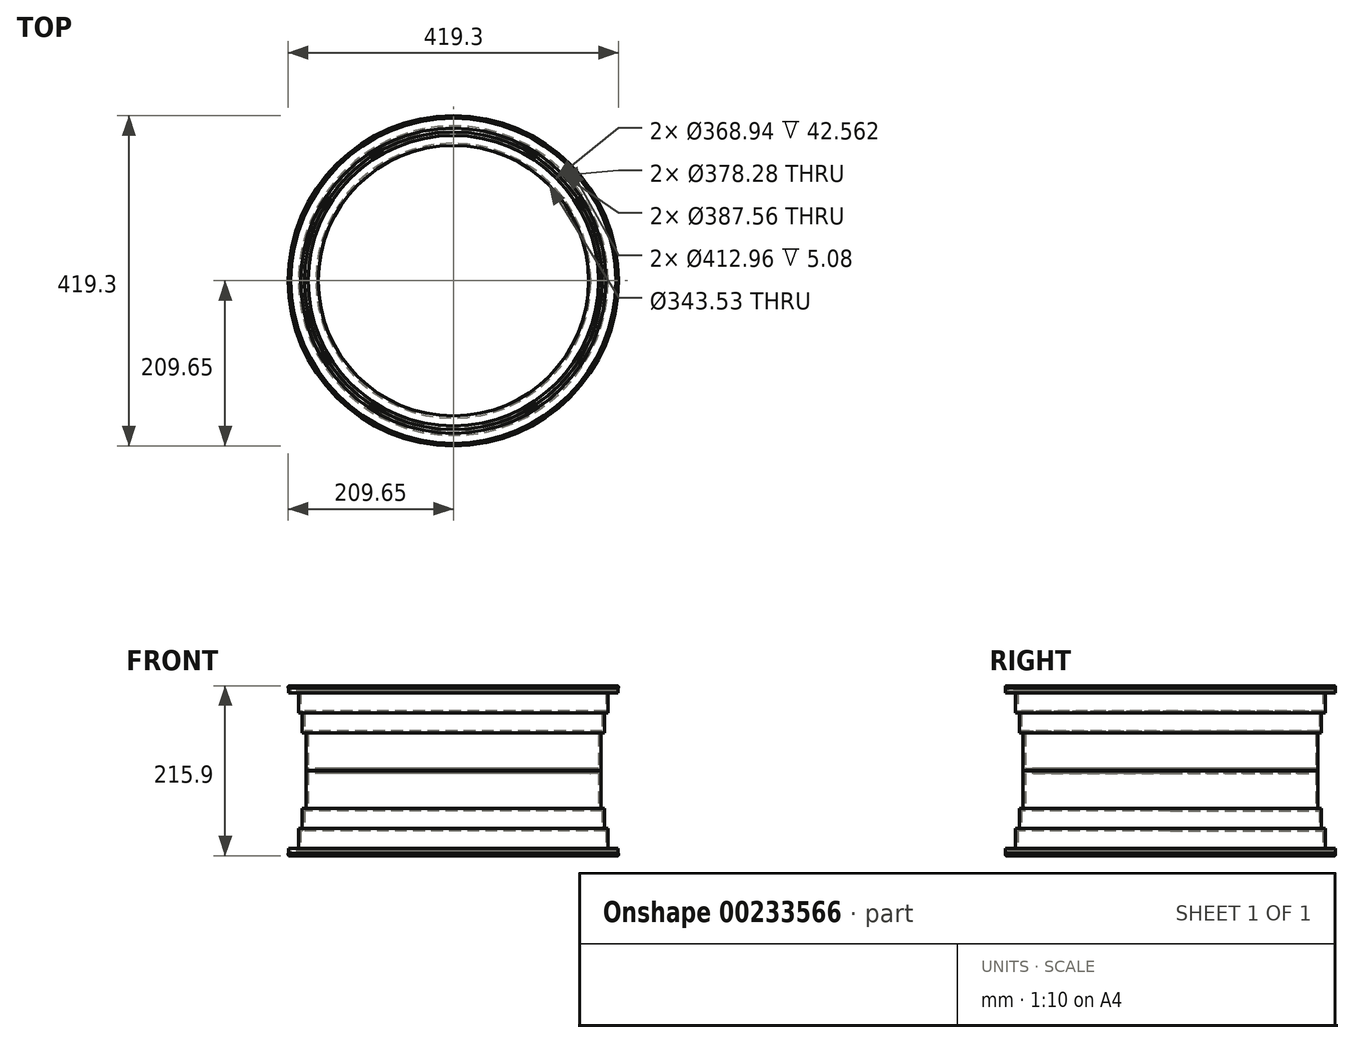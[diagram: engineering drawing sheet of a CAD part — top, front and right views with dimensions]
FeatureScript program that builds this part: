
annotation { "Feature Type Name" : "Feature", "Feature Type Description" : "" }
export const myFeature = defineFeature(function(context is Context, id is Id, definition is map)
    precondition{}
    {
        {
            var Q0;
            Q0=qCreatedBy(makeId("Top.planeOp"),FACE);
            var sketch = newSketch(context, id + "F0", { "sketchPlane" : qUnion([Q0])});
            skCircle(sketch, "E0", {"center": v(0, 0) * mm, "radius": 184.47 * mm});
            skCircle(sketch, "E1.0", {"center": v(0, 0) * mm, "radius": 171.77 * mm});
            skCircle(sketch, "E2", {"center": v(0, 0) * mm, "radius": 189.14 * mm});
            skCircle(sketch, "E3", {"center": v(0, 0) * mm, "radius": 193.78 * mm});
            skCircle(sketch, "E4.0", {"center": v(0, 0) * mm, "radius": 206.48 * mm});
            skCircle(sketch, "E5.0", {"center": v(0, 0) * mm, "radius": 209.65 * mm});
            skSolve(sketch);
        }
        {
            var Q0;
            Q0=makeQuery(id+"F0.imprint","IMPRINT",FACE,{"disambiguationData":[TD([[makeQuery(id+"F0.imprint","IMPRINT",EDGE,{"derivedFrom":sQuery(id+"F0.wireOp",EDGE,"E0")}),1.0]])]});
            var Q1;
            Q1=makeQuery(id+"F0.imprint","IMPRINT",FACE,{"disambiguationData":[TD([[makeQuery(id+"F0.imprint","IMPRINT",EDGE,{"derivedFrom":sQuery(id+"F0.wireOp",EDGE,"E0")}),-1.0]])]});
            extrude(context, id + "F1", {"entities" : qUnion([Q0, Q1]), "endBound" : BoundingType.SYMMETRIC, "depth" : 6.35 * mm});
        }
        {
            var Q0;
            Q0=makeQuery(id+"F0.imprint","IMPRINT",FACE,{"disambiguationData":[TD([[makeQuery(id+"F0.imprint","IMPRINT",EDGE,{"derivedFrom":sQuery(id+"F0.wireOp",EDGE,"E0")}),-1.0]])]});
            extrude(context, id + "F2", {"entities" : qUnion([Q0]), "operationType" : NewBodyOperationType.ADD, "endBound" : BoundingType.SYMMETRIC, "depth" : 101.6 * mm});
        }
        {
            var Q0;
            Q0=makeQuery(id+"F0.imprint","IMPRINT",FACE,{"disambiguationData":[TD([[makeQuery(id+"F0.imprint","IMPRINT",EDGE,{"derivedFrom":sQuery(id+"F0.wireOp",EDGE,"E2")}),-1.0]])]});
            extrude(context, id + "F3", {"entities" : qUnion([Q0]), "operationType" : NewBodyOperationType.ADD, "endBound" : BoundingType.SYMMETRIC, "depth" : 152.4 * mm});
        }
        {
            var Q0;
            Q0=makeQuery(id+"F0.imprint","IMPRINT",FACE,{"disambiguationData":[TD([[makeQuery(id+"F0.imprint","IMPRINT",EDGE,{"derivedFrom":sQuery(id+"F0.wireOp",EDGE,"E3")}),-1.0]])]});
            extrude(context, id + "F4", {"entities" : qUnion([Q0]), "operationType" : NewBodyOperationType.ADD, "endBound" : BoundingType.SYMMETRIC, "depth" : 203.2 * mm});
        }
        {
            var Q0;
            Q0=makeQuery(id+"F0.imprint","IMPRINT",FACE,{"disambiguationData":[TD([[makeQuery(id+"F0.imprint","IMPRINT",EDGE,{"derivedFrom":sQuery(id+"F0.wireOp",EDGE,"E4.0")}),-1.0]])]});
            extrude(context, id + "F5", {"entities" : qUnion([Q0]), "operationType" : NewBodyOperationType.ADD, "endBound" : BoundingType.SYMMETRIC, "depth" : 215.9 * mm});
        }
        {
            var Q0;
            Q0=makeQuery(id+"F5.opExtrude","SWEPT_FACE",FACE,{"disambiguationData":[OSD([sQuery(id+"F0.wireOp",EDGE,"E5.0")])]});
            shell(context, id + "F6", {"entities" : qUnion([Q0]), "thickness" : 2.86 * mm});
        }
        {
            var Q0;
            Q0=makeQuery(id+"F2.opExtrude","CAP_EDGE",EDGE,{"disambiguationData":[OSD([sQuery(id+"F0.wireOp",EDGE,"E0")])],"isStart":true});
            var Q1;
            Q1=makeQuery(id+"F3.opExtrude","CAP_EDGE",EDGE,{"disambiguationData":[OSD([sQuery(id+"F0.wireOp",EDGE,"E2")])],"isStart":true});
            fillet(context, id + "F7", {"entities" : qUnion([Q0, Q1]), "radius" : 5.08 * mm, "tangentPropagation" : true, "allowEdgeOverflow" : false});
        }
        {
            var Q0;
            Q0=makeQuery(id+"F1.opExtrude","CAP_EDGE",EDGE,{"disambiguationData":[OSD([sQuery(id+"F0.wireOp",EDGE,"E1.0")])],"isStart":true});
            fillet(context, id + "F8", {"entities" : qUnion([Q0]), "radius" : 2.54 * mm, "tangentPropagation" : true, "allowEdgeOverflow" : false});
        }
        {
            var Q0;
            Q0=makeQuery(id+"F1.opExtrude","CAP_EDGE",EDGE,{"disambiguationData":[OSD([sQuery(id+"F0.wireOp",EDGE,"E1.0")])],"isStart":false});
            fillet(context, id + "F9", {"entities" : qUnion([Q0]), "radius" : 2.54 * mm, "tangentPropagation" : true, "allowEdgeOverflow" : false});
        }
        {
            var Q0;
            Q0=makeQuery(id+"F2.opExtrude","CAP_EDGE",EDGE,{"disambiguationData":[OSD([sQuery(id+"F0.wireOp",EDGE,"E0")])],"isStart":false});
            var Q1;
            Q1=makeQuery(id+"F3.opExtrude","CAP_EDGE",EDGE,{"disambiguationData":[OSD([sQuery(id+"F0.wireOp",EDGE,"E2")])],"isStart":false});
            fillet(context, id + "F10", {"entities" : qUnion([Q0, Q1]), "radius" : 5.08 * mm, "tangentPropagation" : true, "allowEdgeOverflow" : false});
        }
        {
            var Q0;
            Q0=makeQuery(id+"F4.opExtrude","CAP_EDGE",EDGE,{"disambiguationData":[OSD([sQuery(id+"F0.wireOp",EDGE,"E3")])],"isStart":true});
            fillet(context, id + "F11", {"entities" : qUnion([Q0]), "radius" : 1.9 * mm, "tangentPropagation" : true, "allowEdgeOverflow" : false});
        }
        {
            var Q0;
            Q0=makeQuery(id+"F4.opExtrude","CAP_EDGE",EDGE,{"disambiguationData":[OSD([sQuery(id+"F0.wireOp",EDGE,"E3")])],"isStart":false});
            fillet(context, id + "F12", {"entities" : qUnion([Q0]), "radius" : 1.9 * mm, "tangentPropagation" : true, "allowEdgeOverflow" : false});
        }
        {
            var Q0;
            Q0=makeQuery(id+"F5.opExtrude","CAP_EDGE",EDGE,{"disambiguationData":[OSD([sQuery(id+"F0.wireOp",EDGE,"E4.0")])],"isStart":false});
            var Q1;
            Q1=makeQuery(id+"F5.opExtrude","CAP_EDGE",EDGE,{"disambiguationData":[OSD([sQuery(id+"F0.wireOp",EDGE,"E5.0")])],"isStart":false});
            var Q2;
            Q2=makeQuery(id+"F5.opExtrude","CAP_EDGE",EDGE,{"disambiguationData":[OSD([sQuery(id+"F0.wireOp",EDGE,"E5.0")])],"isStart":true});
            var Q3;
            Q3=makeQuery(id+"F5.opExtrude","CAP_EDGE",EDGE,{"disambiguationData":[OSD([sQuery(id+"F0.wireOp",EDGE,"E4.0")])],"isStart":true});
            fillet(context, id + "F13", {"entities" : qUnion([Q0, Q1, Q2, Q3]), "radius" : 1.27 * mm, "tangentPropagation" : true, "allowEdgeOverflow" : false});
        }
    });
